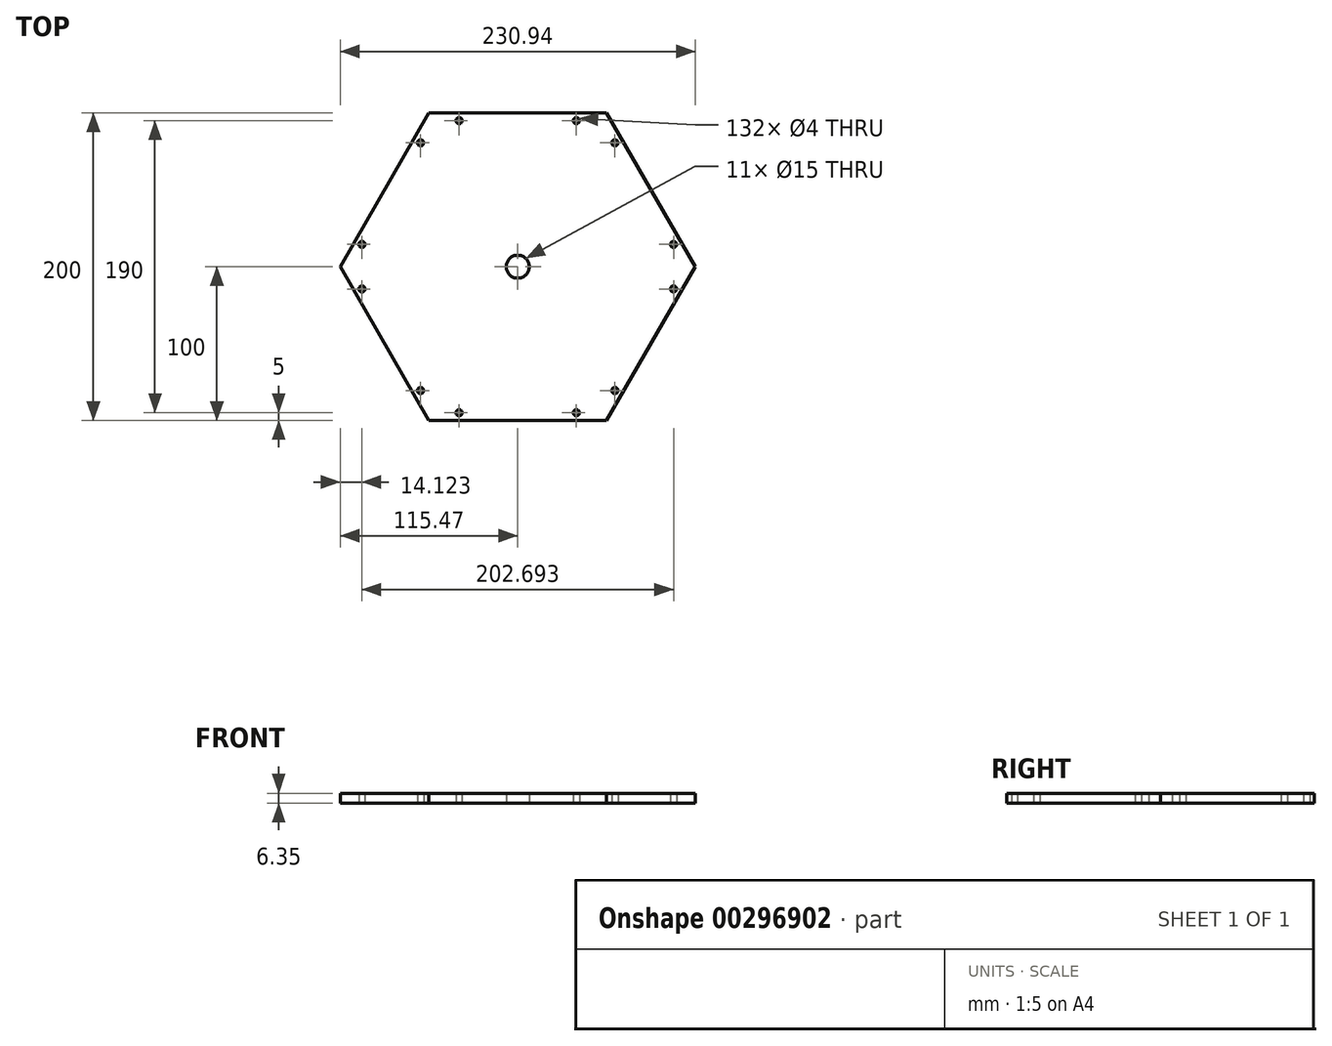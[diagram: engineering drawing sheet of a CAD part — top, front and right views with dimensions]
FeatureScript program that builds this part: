
annotation { "Feature Type Name" : "Feature", "Feature Type Description" : "" }
export const myFeature = defineFeature(function(context is Context, id is Id, definition is map)
    precondition{}
    {
        {
            var Q0;
            Q0=qCreatedBy(makeId("Top.planeOp"),FACE);
            var sketch = newSketch(context, id + "F0", { "sketchPlane" : qUnion([Q0])});
            skCircle(sketch, "E0", {"center": v(0, 0) * mm, "radius": 100 * mm});
            skCircle(sketch, "E1.cCircle", {"center": v(0, 0) * mm, "radius": 100 * mm, "construction": true});
            skLineSegment(sketch, "E1.0", {"start": v(-57.74, 100) * mm, "end": v(57.74, 100) * mm});
            skLineSegment(sketch, "E1.1", {"start": v(57.74, 100) * mm, "end": v(115.47, 0) * mm});
            skLineSegment(sketch, "E1.2", {"start": v(115.47, 0) * mm, "end": v(57.74, -100) * mm});
            skLineSegment(sketch, "E1.3", {"start": v(57.74, -100) * mm, "end": v(-57.74, -100) * mm});
            skLineSegment(sketch, "E1.4", {"start": v(-57.74, -100) * mm, "end": v(-115.47, 0) * mm});
            skLineSegment(sketch, "E1.5", {"start": v(-115.47, 0) * mm, "end": v(-57.74, 100) * mm});
            skPoint(sketch, "E1.0.midPoint", {"position": v(0, 100) * mm});
            skSolve(sketch);
        }
        {
            var Q0;
            Q0=qSketchRegion(id+"F0",true);
            extrude(context, id + "F1", {"entities" : qUnion([Q0]), "depth" : 6.35 * mm});
        }
        {
            var Q0;
            Q0=qCreatedBy(makeId("Top.planeOp"),FACE);
            var sketch = newSketch(context, id + "F2", { "sketchPlane" : qUnion([Q0])});
            skCircle(sketch, "E2.cCircle", {"center": v(0, 0) * mm, "radius": 95 * mm, "construction": true});
            skLineSegment(sketch, "E2.0", {"start": v(-54.85, 95) * mm, "end": v(54.85, 95) * mm, "construction": true});
            skLineSegment(sketch, "E2.1", {"start": v(54.85, 95) * mm, "end": v(109.7, 0) * mm, "construction": true});
            skLineSegment(sketch, "E2.2", {"start": v(109.7, 0) * mm, "end": v(54.85, -95) * mm, "construction": true});
            skLineSegment(sketch, "E2.3", {"start": v(54.85, -95) * mm, "end": v(-54.85, -95) * mm, "construction": true});
            skLineSegment(sketch, "E2.4", {"start": v(-54.85, -95) * mm, "end": v(-109.7, 0) * mm, "construction": true});
            skLineSegment(sketch, "E2.5", {"start": v(-109.7, 0) * mm, "end": v(-54.85, 95) * mm, "construction": true});
            skPoint(sketch, "E2.0.midPoint", {"position": v(0, 95) * mm});
            skPoint(sketch, "E3", {"position": v(38.15, 95) * mm});
            skPoint(sketch, "E4", {"position": v(-38.15, 95) * mm});
            skPoint(sketch, "E5", {"position": v(38.15, -95) * mm});
            skPoint(sketch, "E6", {"position": v(-38.15, -95) * mm});
            skPoint(sketch, "E7", {"position": v(-63.2, -80.54) * mm});
            skPoint(sketch, "E8", {"position": v(-101.35, -14.46) * mm});
            skPoint(sketch, "E9", {"position": v(-101.35, 14.46) * mm});
            skPoint(sketch, "E10", {"position": v(-63.2, 80.54) * mm});
            skPoint(sketch, "E11", {"position": v(63.2, 80.54) * mm});
            skPoint(sketch, "E12", {"position": v(101.35, 14.46) * mm});
            skPoint(sketch, "E13", {"position": v(101.35, -14.46) * mm});
            skPoint(sketch, "E14", {"position": v(63.2, -80.54) * mm});
            skCircle(sketch, "E15", {"center": v(38.15, 95) * mm, "radius": 2 * mm});
            skCircle(sketch, "E16", {"center": v(-38.15, 95) * mm, "radius": 2 * mm});
            skCircle(sketch, "E17", {"center": v(-63.2, 80.54) * mm, "radius": 2 * mm});
            skCircle(sketch, "E18", {"center": v(-101.35, 14.46) * mm, "radius": 2 * mm});
            skCircle(sketch, "E19", {"center": v(-101.35, -14.46) * mm, "radius": 2 * mm});
            skCircle(sketch, "E20", {"center": v(-63.2, -80.54) * mm, "radius": 2 * mm});
            skCircle(sketch, "E21", {"center": v(-38.15, -95) * mm, "radius": 2 * mm});
            skCircle(sketch, "E22", {"center": v(38.15, -95) * mm, "radius": 2 * mm});
            skCircle(sketch, "E23", {"center": v(63.2, -80.54) * mm, "radius": 2 * mm});
            skCircle(sketch, "E24", {"center": v(101.35, -14.46) * mm, "radius": 2 * mm});
            skCircle(sketch, "E25", {"center": v(101.35, 14.46) * mm, "radius": 2 * mm});
            skCircle(sketch, "E26", {"center": v(63.2, 80.54) * mm, "radius": 2 * mm});
            skSolve(sketch);
        }
        {
            var Q0;
            Q0=qSketchRegion(id+"F2",true);
            extrude(context, id + "F3", {"entities" : qUnion([Q0]), "operationType" : NewBodyOperationType.REMOVE, "depth" : 20000 * mm});
        }
        {
            var Q0;
            Q0=qCreatedBy(makeId("Top.planeOp"),FACE);
            var sketch = newSketch(context, id + "F4", { "sketchPlane" : qUnion([Q0])});
            skCircle(sketch, "E27", {"center": v(0, 0) * mm, "radius": 7.5 * mm});
            skSolve(sketch);
        }
        {
            var Q0;
            Q0 = qSketchRegion(id + "F4", true);
            extrude(context, id + "F5", {"entities" : qUnion([Q0]), "operationType" : NewBodyOperationType.REMOVE, "depth" : 55.3 * mm});
        }
    });
